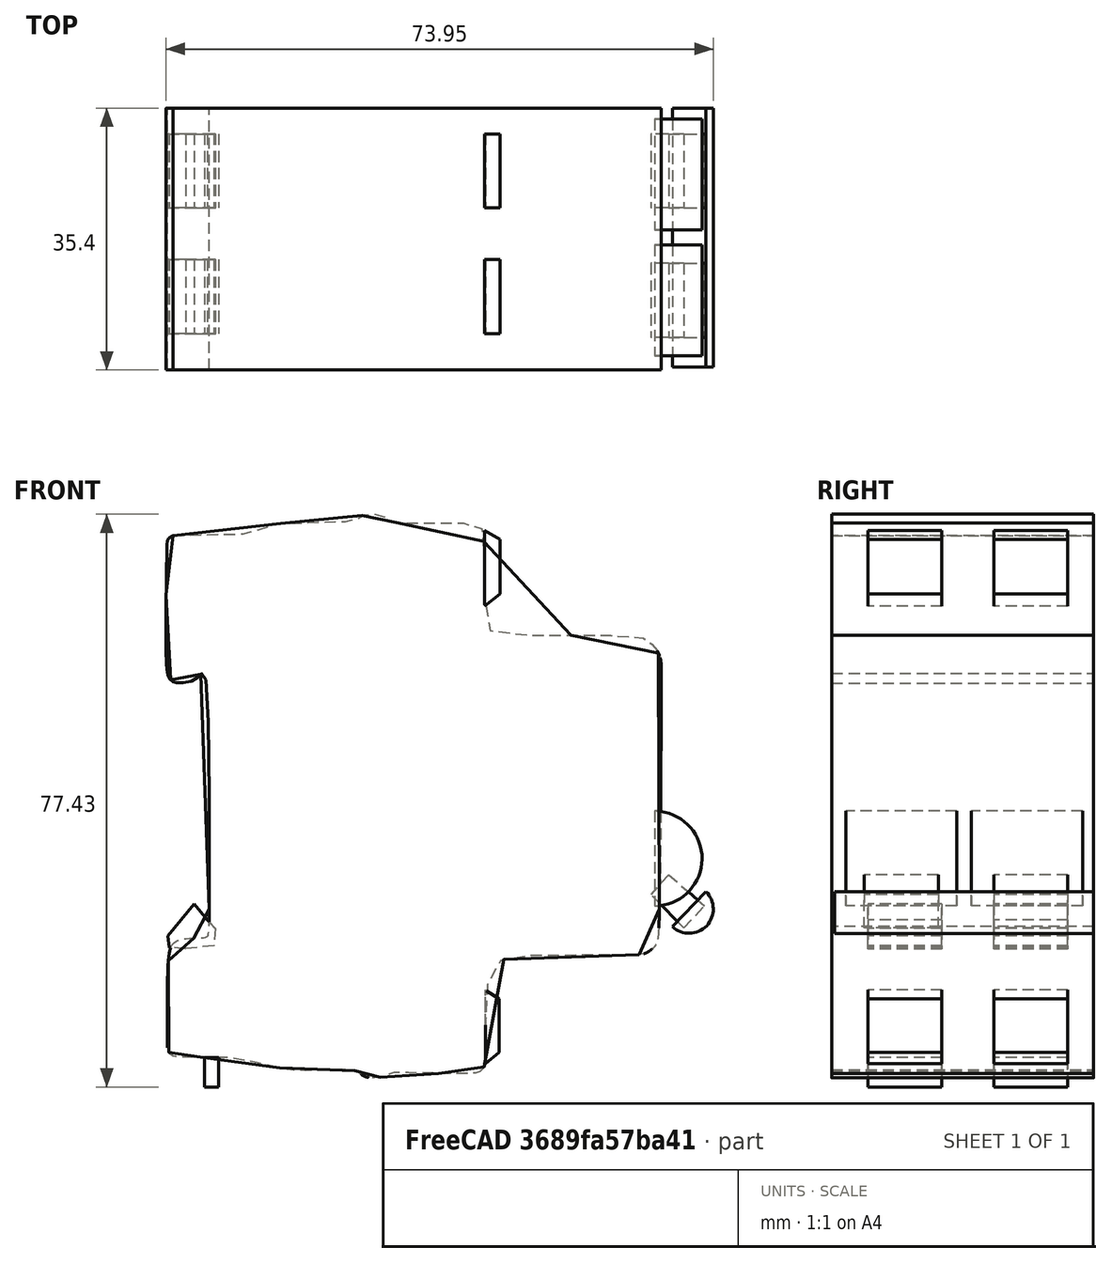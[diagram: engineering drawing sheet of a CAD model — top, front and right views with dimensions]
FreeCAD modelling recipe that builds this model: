
FCSTD DOCUMENT  (FreeCAD 1.1R20260325 (Git shallow))
Label: Disjuntor_Bifasio
License: All rights reserved
LicenseURL: http://en.wikipedia.org/wiki/All_rights_reserved
objects: Sketcher::SketchObject×8, Part::Extrusion×8, Part::Compound×3
note: 27 computed .brp shape members not serialized (recipe doc carries the construction recipe); baked Part::Feature solids carry a one-line shape summary decoded from their .brp

FEATURE [Sketcher::SketchObject] Sketch019
  ArcFitTolerance = 0
  ExternalTypes = [0]
  FullyConstrained = false
  MakeInternals = false
  MapMode = 2
  Placement = pos=(0,0,1.5) rot=(0,0,1;0rad)
  _ExternalGeoVersion = 0
  sketch-geometry (4):
    g0: LineSegment StartX=27.2958 StartY=-25.5037 StartZ=0 EndX=32.1116 EndY=-29.7175 EndZ=0
    g1: LineSegment StartX=29.3597 StartY=-32.7274 StartZ=0 EndX=32.1116 EndY=-29.7175 EndZ=0
    g2: LineSegment StartX=29.3597 StartY=-32.7274 StartZ=0 EndX=24.8878 EndY=-28.1696 EndZ=0
    g3: LineSegment StartX=27.2958 StartY=-25.5037 StartZ=0 EndX=24.8878 EndY=-28.1696 EndZ=0
  constraints (4):
    c: Coincident(g1,g0)
    c: Coincident(g2,g1)
    c: Coincident(g3,g0)
    c: Coincident(g3,g2)
FEATURE [Part::Extrusion] Extrude007
  Base = -> Sketch019
  Dir = (0,0,1)
  DirMode = 2
  FaceMakerClass = Part::FaceMakerBullseye
  FaceMakerMode = 3
  InnerWireTaper = 0
  LengthFwd = 10
  LengthRev = 0
  Placement = pos=(0,0.3,19.5) rot=(0,0,1;0rad)
  Solid = true
  Symmetric = false
FEATURE [Sketcher::SketchObject] Sketch024
  ArcFitTolerance = 0
  ExternalTypes = [0]
  FullyConstrained = false
  MakeInternals = false
  _ExternalGeoVersion = 0
  sketch-geometry (2):
    g0: LineSegment StartX=25.3967 StartY=-16.6078 StartZ=0 EndX=25.3967 EndY=-29.437 EndZ=0
    g1: ArcOfCircle CenterX=25.3967 CenterY=-23.0224 CenterZ=0 NormalX=0 NormalY=0 NormalZ=1 AngleXU=0 Radius=6.41461 StartAngle=4.71239 EndAngle=7.85398
  constraints (4):
    c: Vertical(g0)
    c: PointOnObject(g1,g0)
    c: Coincident(g1,g0)
    c: Coincident(g1,g0)
FEATURE [Sketcher::SketchObject] Sketch022
  ArcFitTolerance = 0
  ExternalTypes = [0]
  FullyConstrained = false
  MakeInternals = false
  _ExternalGeoVersion = 0
  sketch-geometry (157):
    g0-g78: Circle [constr] x79 (B-spline internal-alignment scaffolding for g79; pole/knot coordinates omitted)
    g79: BSplineCurve PolesCount=79 KnotsCount=77 Degree=3 IsPeriodic=0
    g80-g156: GeomPoint [constr] x77 (B-spline internal-alignment scaffolding for g79; pole/knot coordinates omitted)
  constraints (53):
    c: Weight(g0) = 1
    c: Equal(g0, g1-g7) x7
    c: PointOnObject(g7,g6)
    c: Equal(g0,g8)
    c: PointOnObject(g8,g7)
    c: Equal(g0,g9)
    c: Equal(g0,g10)
    c: Equal(g0,g11)
    c: PointOnObject(g11,g10)
    c: Equal(g0,g12)
    c: Equal(g0,g13)
    c: Equal(g0,g14)
    c: PointOnObject(g14,g13)
    c: Equal(g0, g15-g21) x7
    c: PointOnObject(g21,g20)
    c: Equal(g0,g22)
    c: PointOnObject(g22,g21)
    c: Equal(g0, g23-g26) x4
    c: PointOnObject(g26,g25)
    c: Equal(g0,g27)
    c: PointOnObject(g27,g26)
    c: Equal(g0, g28-g39) x12
    c: PointOnObject(g39,g38)
    c: Equal(g0, g40-g43) x4
    c: PointOnObject(g43,g42)
    c: Equal(g0,g44)
    c: PointOnObject(g44,g43)
    c: Equal(g0, g45-g50) x6
    c: PointOnObject(g50,g49)
    c: Equal(g0, g51-g56) x6
    c: PointOnObject(g56,g55)
    c: Equal(g0,g57)
    c: Equal(g0,g58)
    c: Equal(g0,g59)
    c: PointOnObject(g59,g58)
    c: Equal(g0,g60)
    c: PointOnObject(g60,g59)
    c: Equal(g0, g61-g67) x7
    c: PointOnObject(g67,g66)
    c: Equal(g0, g68-g71) x4
    c: PointOnObject(g71,g70)
    c: Equal(g0,g72)
    c: Equal(g0,g73)
    c: PointOnObject(g73,g72)
    c: Equal(g0,g74)
    c: Equal(g0,g75)
    c: Equal(g0,g76)
    c: PointOnObject(g76,g0)
    c: Equal(g0,g77)
    c: Equal(g0,g78)
    c: Coincident(g78,g0)
    c: InternalAlignment(g0-g78 -> g79) x79
    c: InternalAlignment(g80-g156 -> g79) x77
FEATURE [Sketcher::SketchObject] Sketch023
  ArcFitTolerance = 0
  ExternalTypes = [0]
  FullyConstrained = false
  MakeInternals = false
  MapMode = 2
  _ExternalGeoVersion = 0
  sketch-geometry (19):
    g0: LineSegment StartX=2.43973 StartY=21.3388 StartZ=0 EndX=2.43973 EndY=11.099 EndZ=0
    g1: LineSegment StartX=2.43973 StartY=11.099 StartZ=0 EndX=4.52634 EndY=12.7606 EndZ=0
    g2: LineSegment StartX=4.52634 StartY=12.7606 StartZ=0 EndX=4.52634 EndY=20.1023 EndZ=0
    g3: LineSegment StartX=4.52634 StartY=20.1023 StartZ=0 EndX=2.43973 EndY=21.3388 EndZ=0
    g4: LineSegment StartX=2.56636 StartY=-50.7191 StartZ=0 EndX=2.56636 EndY=-40.8041 EndZ=0
    g5: LineSegment StartX=2.56636 StartY=-40.8041 StartZ=0 EndX=4.41102 EndY=-42.0146 EndZ=0
    g6: LineSegment StartX=4.41102 StartY=-42.0146 StartZ=0 EndX=4.41102 EndY=-49.2203 EndZ=0
    g7: LineSegment StartX=4.41102 StartY=-49.2203 StartZ=0 EndX=2.56636 EndY=-50.7191 EndZ=0
    g8: LineSegment StartX=-35.4006 StartY=-49.9211 StartZ=0 EndX=-33.4983 EndY=-49.9211 EndZ=0
    g9: LineSegment StartX=-33.4983 StartY=-49.9211 StartZ=0 EndX=-33.4983 EndY=-53.8986 EndZ=0
    g10: LineSegment StartX=-33.4983 StartY=-53.8986 StartZ=0 EndX=-35.4006 EndY=-53.8986 EndZ=0
    g11: LineSegment StartX=-35.4006 StartY=-53.8986 StartZ=0 EndX=-35.4006 EndY=-49.9211 EndZ=0
    g12: LineSegment StartX=-40.1754 StartY=-35.0337 StartZ=0 EndX=-40.3686 EndY=-33.488 EndZ=0
    g13: LineSegment StartX=-40.3686 StartY=-33.488 StartZ=0 EndX=-36.8136 EndY=-29.1602 EndZ=0
    g14: LineSegment StartX=-36.8136 StartY=-29.1602 StartZ=0 EndX=-35.0361 EndY=-31.3241 EndZ=0
    g15: LineSegment StartX=-35.0361 StartY=-31.3241 StartZ=0 EndX=-33.9928 EndY=-32.4834 EndZ=0
    g16: LineSegment StartX=-33.9928 StartY=-32.4834 StartZ=0 EndX=-34.186 EndY=-34.8018 EndZ=0
    g17: LineSegment StartX=-34.186 StartY=-34.8018 StartZ=0 EndX=-37.9728 EndY=-35.2269 EndZ=0
    g18: LineSegment StartX=-37.9728 StartY=-35.2269 StartZ=0 EndX=-40.1754 EndY=-35.0337 EndZ=0
  constraints (27):
    c: Vertical(g0)
    c: Coincident(g0,g1)
    c: Coincident(g1,g2)
    c: Vertical(g2)
    c: Coincident(g2,g3)
    c: Coincident(g3,g0)
    c: Vertical(g4)
    c: Coincident(g4,g5)
    c: Coincident(g5,g6)
    c: Vertical(g6)
    c: Coincident(g6,g7)
    c: Coincident(g7,g4)
    c: Horizontal(g8)
    c: Coincident(g8,g9)
    c: Vertical(g9)
    c: Coincident(g9,g10)
    c: Horizontal(g10)
    c: Coincident(g10,g11)
    c: Coincident(g11,g8)
    c: Vertical(g11)
    c: Coincident(g12,g13)
    c: Coincident(g13,g14)
    c: Coincident(g14,g15)
    c: Coincident(g15,g16)
    c: Coincident(g16,g17)
    c: Coincident(g17,g18)
    c: Coincident(g18,g12)
FEATURE [Part::Extrusion] Extrude008
  Base = -> Sketch023
  Dir = (0,0,1)
  DirMode = 2
  FaceMakerClass = Part::FaceMakerBullseye
  FaceMakerMode = 3
  InnerWireTaper = 0
  LengthFwd = 10
  LengthRev = 0
  Placement = pos=(0,0,20.5) rot=(0,0,1;0rad)
  Solid = true
  Symmetric = false
FEATURE [Part::Extrusion] Extrude012
  Base = -> Sketch022
  Dir = (0,0,1)
  DirMode = 2
  FaceMakerClass = Part::FaceMakerBullseye
  FaceMakerMode = 3
  InnerWireTaper = 0
  LengthFwd = 35.4
  LengthRev = 0
  Solid = true
  Symmetric = false
FEATURE [Sketcher::SketchObject] Sketch021
  ArcFitTolerance = 0
  ExternalTypes = [0]
  FullyConstrained = false
  MakeInternals = false
  _ExternalGeoVersion = 0
  sketch-geometry (2):
    g0: LineSegment StartX=25.3967 StartY=-16.6078 StartZ=0 EndX=25.3967 EndY=-29.437 EndZ=0
    g1: ArcOfCircle CenterX=25.3967 CenterY=-23.0224 CenterZ=0 NormalX=0 NormalY=0 NormalZ=1 AngleXU=0 Radius=6.41461 StartAngle=4.71239 EndAngle=7.85398
  constraints (4):
    c: Vertical(g0)
    c: PointOnObject(g1,g0)
    c: Coincident(g1,g0)
    c: Coincident(g1,g0)
FEATURE [Part::Extrusion] Extrude013
  Base = -> Sketch021
  Dir = (0,0,1)
  DirMode = 2
  FaceMakerClass = Part::FaceMakerBullseye
  FaceMakerMode = 3
  InnerWireTaper = 0
  LengthFwd = 15
  LengthRev = 0
  Placement = pos=(0,0,18.5) rot=(0,0,1;0rad)
  Solid = true
  Symmetric = false
FEATURE [Part::Extrusion] Extrude010
  Base = -> Sketch024
  Dir = (0,0,1)
  DirMode = 2
  FaceMakerClass = Part::FaceMakerBullseye
  FaceMakerMode = 3
  InnerWireTaper = 0
  LengthFwd = 15
  LengthRev = 0
  Placement = pos=(0,0,1.5) rot=(0,0,1;0rad)
  Solid = true
  Symmetric = false
FEATURE [Sketcher::SketchObject] Sketch026
  ArcFitTolerance = 0
  AttachmentSupport = -> [Extrude010]
  ExternalTypes = [0]
  FullyConstrained = false
  MakeInternals = false
  MapMode = 2
  Placement = pos=(0,0,1.5) rot=(0,0,1;0rad)
  _ExternalGeoVersion = 0
  sketch-geometry (4):
    g0: LineSegment StartX=27.2958 StartY=-25.5037 StartZ=0 EndX=32.1116 EndY=-29.7175 EndZ=0
    g1: LineSegment StartX=29.3597 StartY=-32.7274 StartZ=0 EndX=32.1116 EndY=-29.7175 EndZ=0
    g2: LineSegment StartX=29.3597 StartY=-32.7274 StartZ=0 EndX=24.8878 EndY=-28.1696 EndZ=0
    g3: LineSegment StartX=27.2958 StartY=-25.5037 StartZ=0 EndX=24.8878 EndY=-28.1696 EndZ=0
  constraints (4):
    c: Coincident(g1,g0)
    c: Coincident(g2,g1)
    c: Coincident(g3,g0)
    c: Coincident(g3,g2)
FEATURE [Part::Extrusion] Extrude005
  Base = -> Sketch026
  Dir = (0,0,1)
  DirMode = 2
  FaceMakerClass = Part::FaceMakerBullseye
  FaceMakerMode = 3
  InnerWireTaper = 0
  LengthFwd = 10
  LengthRev = 0
  Placement = pos=(0,0.3,2) rot=(0,0,1;0rad)
  Solid = true
  Symmetric = false
FEATURE [Sketcher::SketchObject] Sketch020
  ArcFitTolerance = 0
  ExternalTypes = [0]
  FullyConstrained = false
  MakeInternals = false
  _ExternalGeoVersion = 0
  sketch-geometry (2):
    g0: LineSegment StartX=27.7904 StartY=-32.2195 StartZ=0 EndX=32.3224 EndY=-27.4829 EndZ=0
    g1: ArcOfCircle CenterX=30.0564 CenterY=-29.8512 CenterZ=0 NormalX=0 NormalY=0 NormalZ=1 AngleXU=0 Radius=3.27775 StartAngle=3.94906 EndAngle=7.09065
  constraints (3):
    c: PointOnObject(g1,g0)
    c: Coincident(g1,g0)
    c: Coincident(g1,g0)
FEATURE [Part::Extrusion] Extrude009
  Base = -> Sketch020
  Dir = (0,0,1)
  DirMode = 2
  FaceMakerClass = Part::FaceMakerBullseye
  FaceMakerMode = 3
  InnerWireTaper = 0
  LengthFwd = 35
  LengthRev = 0
  Solid = true
  Symmetric = false
FEATURE [Sketcher::SketchObject] Sketch025
  ArcFitTolerance = 0
  AttachmentSupport = -> [Extrude012]
  ExternalTypes = [0]
  FullyConstrained = false
  MakeInternals = false
  MapMode = 2
  _ExternalGeoVersion = 0
  sketch-geometry (19):
    g0: LineSegment StartX=2.43973 StartY=21.3388 StartZ=0 EndX=2.43973 EndY=11.099 EndZ=0
    g1: LineSegment StartX=2.43973 StartY=11.099 StartZ=0 EndX=4.52634 EndY=12.7606 EndZ=0
    g2: LineSegment StartX=4.52634 StartY=12.7606 StartZ=0 EndX=4.52634 EndY=20.1023 EndZ=0
    g3: LineSegment StartX=4.52634 StartY=20.1023 StartZ=0 EndX=2.43973 EndY=21.3388 EndZ=0
    g4: LineSegment StartX=2.56636 StartY=-50.7191 StartZ=0 EndX=2.56636 EndY=-40.8041 EndZ=0
    g5: LineSegment StartX=2.56636 StartY=-40.8041 StartZ=0 EndX=4.41102 EndY=-42.0146 EndZ=0
    g6: LineSegment StartX=4.41102 StartY=-42.0146 StartZ=0 EndX=4.41102 EndY=-49.2203 EndZ=0
    g7: LineSegment StartX=4.41102 StartY=-49.2203 StartZ=0 EndX=2.56636 EndY=-50.7191 EndZ=0
    g8: LineSegment StartX=-35.4006 StartY=-49.9211 StartZ=0 EndX=-33.4983 EndY=-49.9211 EndZ=0
    g9: LineSegment StartX=-33.4983 StartY=-49.9211 StartZ=0 EndX=-33.4983 EndY=-53.8986 EndZ=0
    g10: LineSegment StartX=-33.4983 StartY=-53.8986 StartZ=0 EndX=-35.4006 EndY=-53.8986 EndZ=0
    g11: LineSegment StartX=-35.4006 StartY=-53.8986 StartZ=0 EndX=-35.4006 EndY=-49.9211 EndZ=0
    g12: LineSegment StartX=-40.1754 StartY=-35.0337 StartZ=0 EndX=-40.3686 EndY=-33.488 EndZ=0
    g13: LineSegment StartX=-40.3686 StartY=-33.488 StartZ=0 EndX=-36.8136 EndY=-29.1602 EndZ=0
    g14: LineSegment StartX=-36.8136 StartY=-29.1602 StartZ=0 EndX=-35.0361 EndY=-31.3241 EndZ=0
    g15: LineSegment StartX=-35.0361 StartY=-31.3241 StartZ=0 EndX=-33.9928 EndY=-32.4834 EndZ=0
    g16: LineSegment StartX=-33.9928 StartY=-32.4834 StartZ=0 EndX=-34.186 EndY=-34.8018 EndZ=0
    g17: LineSegment StartX=-34.186 StartY=-34.8018 StartZ=0 EndX=-37.9728 EndY=-35.2269 EndZ=0
    g18: LineSegment StartX=-37.9728 StartY=-35.2269 StartZ=0 EndX=-40.1754 EndY=-35.0337 EndZ=0
  constraints (27):
    c: Vertical(g0)
    c: Coincident(g0,g1)
    c: Coincident(g1,g2)
    c: Vertical(g2)
    c: Coincident(g2,g3)
    c: Coincident(g3,g0)
    c: Vertical(g4)
    c: Coincident(g4,g5)
    c: Coincident(g5,g6)
    c: Vertical(g6)
    c: Coincident(g6,g7)
    c: Coincident(g7,g4)
    c: Horizontal(g8)
    c: Coincident(g8,g9)
    c: Vertical(g9)
    c: Coincident(g9,g10)
    c: Horizontal(g10)
    c: Coincident(g10,g11)
    c: Coincident(g11,g8)
    c: Vertical(g11)
    c: Coincident(g12,g13)
    c: Coincident(g13,g14)
    c: Coincident(g14,g15)
    c: Coincident(g15,g16)
    c: Coincident(g16,g17)
    c: Coincident(g17,g18)
    c: Coincident(g18,g12)
FEATURE [Part::Extrusion] Extrude011
  Base = -> Sketch025
  Dir = (0,0,1)
  DirMode = 2
  FaceMakerClass = Part::FaceMakerBullseye
  FaceMakerMode = 3
  InnerWireTaper = 0
  LengthFwd = 10
  LengthRev = 0
  Placement = pos=(0,0,3.5) rot=(0,0,1;0rad)
  Solid = true
  Symmetric = false
FEATURE [Part::Compound] Compound  label="Peça"
  Base_StandardCode = 23-35 35 00
  Links = -> [Extrude011,Extrude008,Extrude010,Extrude013,Extrude012]
FEATURE [Part::Compound] Compound001  label="Interruptor"
  Base_StandardCode = 23-35 37 00
  Links = -> [Extrude009,Extrude005,Extrude007]
FEATURE [Part::Compound] Compound002  label="Disjunto_Bi"
  Base_StandardCode = 23-35 35 00
  Links = -> [Compound,Compound001]
  Placement = pos=(0,61.5238,55) rot=(1,0,0;1.5708rad)
